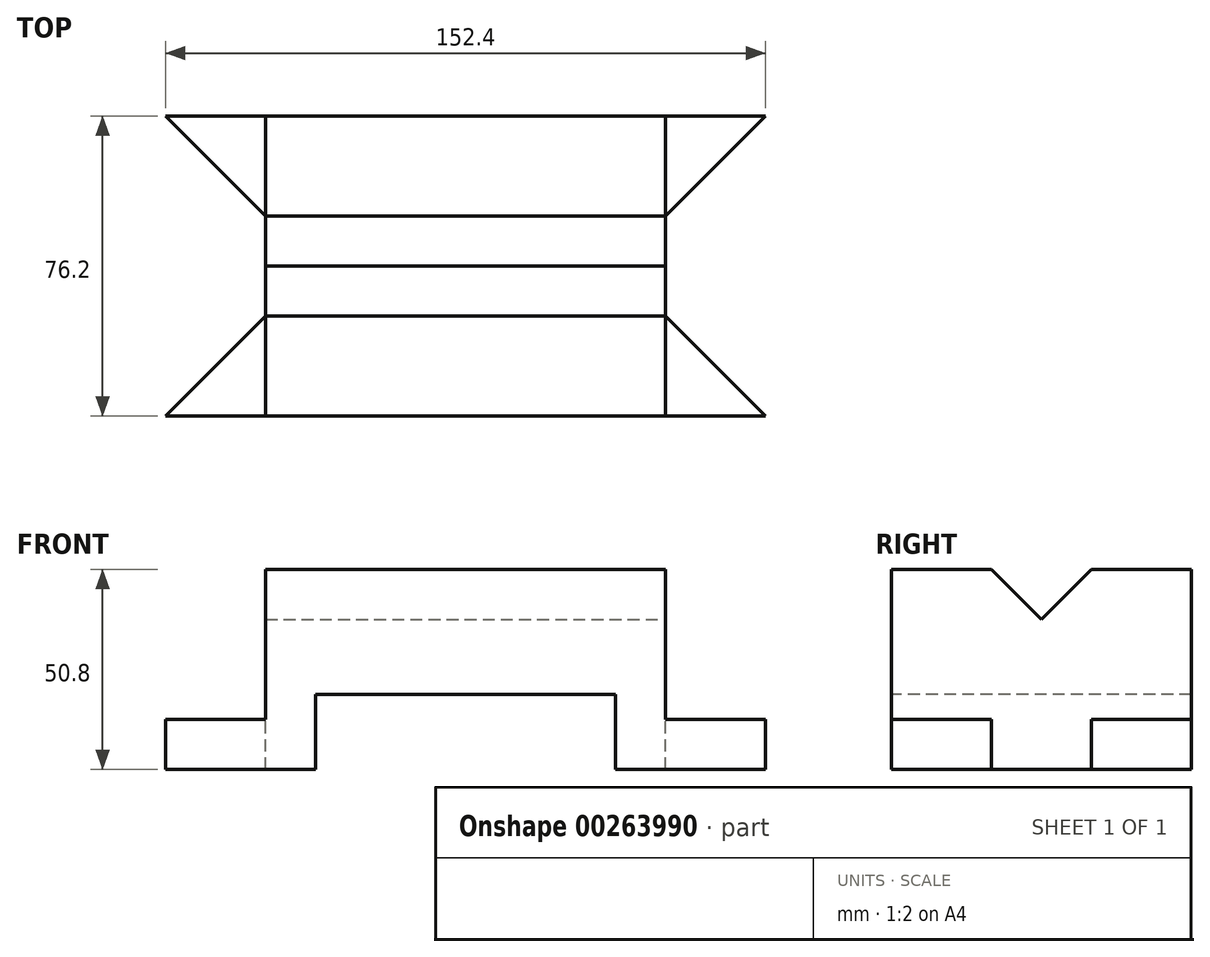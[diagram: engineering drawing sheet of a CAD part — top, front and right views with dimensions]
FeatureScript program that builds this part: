
annotation { "Feature Type Name" : "Feature", "Feature Type Description" : "" }
export const myFeature = defineFeature(function(context is Context, id is Id, definition is map)
    precondition{}
    {
        {
            var Q0;
            Q0=qCreatedBy(makeId("Front.planeOp"),FACE);
            var sketch = newSketch(context, id + "F0", { "sketchPlane" : qUnion([Q0])});
            skLineSegment(sketch, "E0", {"start": v(-76.43, 0) * mm, "end": v(-76.43, 12.7) * mm});
            skLineSegment(sketch, "E1", {"start": v(-76.43, 12.7) * mm, "end": v(-51.03, 12.7) * mm});
            skLineSegment(sketch, "E2", {"start": v(-51.03, 12.7) * mm, "end": v(-51.03, 50.8) * mm});
            skLineSegment(sketch, "E3", {"start": v(-51.03, 50.8) * mm, "end": v(50.57, 50.8) * mm});
            skLineSegment(sketch, "E4", {"start": v(50.57, 50.8) * mm, "end": v(50.57, 12.7) * mm});
            skLineSegment(sketch, "E5", {"start": v(50.57, 12.7) * mm, "end": v(75.97, 12.7) * mm});
            skLineSegment(sketch, "E6", {"start": v(75.97, 12.7) * mm, "end": v(75.97, 0) * mm});
            skLineSegment(sketch, "E7", {"start": v(75.97, 0) * mm, "end": v(37.87, 0) * mm});
            skLineSegment(sketch, "E8", {"start": v(37.87, 0) * mm, "end": v(37.87, 19.05) * mm});
            skLineSegment(sketch, "E9", {"start": v(37.87, 19.05) * mm, "end": v(-38.33, 19.05) * mm});
            skLineSegment(sketch, "E10", {"start": v(-38.33, 19.05) * mm, "end": v(-38.33, 0) * mm});
            skLineSegment(sketch, "E11", {"start": v(-38.33, 0) * mm, "end": v(-76.43, 0) * mm});
            skSolve(sketch);
        }
        {
            var Q0;
            Q0=makeQuery(id+"F0.imprint","IMPRINT",FACE,{"disambiguationData":[TD([[makeQuery(id+"F0.imprint","IMPRINT",EDGE,{"derivedFrom":sQuery(id+"F0.wireOp",EDGE,"E0")}),-1.0]])]});
            extrude(context, id + "F1", {"entities" : qUnion([Q0]), "oppositeDirection" : true, "depth" : 76.2 * mm});
        }
        {
            var Q0;
            Q0=makeQuery(id+"F1.opExtrude","SWEPT_FACE",FACE,{"disambiguationData":[OSD([sQuery(id+"F0.wireOp",EDGE,"E1")])]});
            var sketch = newSketch(context, id + "F2", { "sketchPlane" : qUnion([Q0])});
            skLineSegment(sketch, "E12", {"start": v(-51.03, 0) * mm, "end": v(-51.03, 25.4) * mm});
            skLineSegment(sketch, "E13", {"start": v(-51.03, 25.4) * mm, "end": v(-76.43, 0) * mm});
            skLineSegment(sketch, "E14", {"start": v(-51.03, 76.2) * mm, "end": v(-51.03, 50.8) * mm});
            skLineSegment(sketch, "E15", {"start": v(-51.03, 50.8) * mm, "end": v(-76.43, 76.2) * mm});
            skLineSegment(sketch, "E16", {"start": v(-76.43, 76.2) * mm, "end": v(-51.03, 76.2) * mm});
            skLineSegment(sketch, "E17", {"start": v(-76.43, 0) * mm, "end": v(-51.03, 0) * mm});
            skSolve(sketch);
        }
        {
            var Q0;
            {var subQ0=sQuery(id+"F2.wireOp",EDGE,"E13");Q0=makeQuery(id+"F2.imprint","IMPRINT",FACE,{"disambiguationData":[TD([[makeQuery(id+"F2.imprint","IMPRINT",EDGE,{"derivedFrom":subQ0}),-1.0]])]});}
            extrude(context, id + "F3", {"entities" : qUnion([Q0]), "operationType" : NewBodyOperationType.REMOVE, "endBound" : BoundingType.UP_TO_NEXT, "oppositeDirection" : true, "depth" : 25.4 * mm});
        }
        {
            var Q0;
            Q0=makeQuery(id+"F1.opExtrude","SWEPT_FACE",FACE,{"disambiguationData":[OSD([sQuery(id+"F0.wireOp",EDGE,"E5")])]});
            var sketch = newSketch(context, id + "F4", { "sketchPlane" : qUnion([Q0])});
            skLineSegment(sketch, "E18", {"start": v(50.57, 0) * mm, "end": v(75.97, 0) * mm});
            skLineSegment(sketch, "E19", {"start": v(50.57, 0) * mm, "end": v(50.57, 25.4) * mm});
            skLineSegment(sketch, "E20", {"start": v(50.57, 25.4) * mm, "end": v(75.97, 0) * mm});
            skLineSegment(sketch, "E21", {"start": v(50.57, 76.2) * mm, "end": v(50.57, 50.8) * mm});
            skLineSegment(sketch, "E22", {"start": v(50.57, 50.8) * mm, "end": v(75.97, 76.2) * mm});
            skLineSegment(sketch, "E23", {"start": v(75.97, 76.2) * mm, "end": v(50.57, 76.2) * mm});
            skSolve(sketch);
        }
        {
            var Q0;
            {var subQ0=sQuery(id+"F4.wireOp",EDGE,"E20");Q0=makeQuery(id+"F4.imprint","IMPRINT",FACE,{"disambiguationData":[TD([[makeQuery(id+"F4.imprint","IMPRINT",EDGE,{"derivedFrom":subQ0}),1.0]])]});}
            extrude(context, id + "F5", {"entities" : qUnion([Q0]), "operationType" : NewBodyOperationType.REMOVE, "endBound" : BoundingType.UP_TO_NEXT, "oppositeDirection" : true, "depth" : 25.4 * mm});
        }
        {
            var Q0;
            {var subQ0=sQuery(id+"F0.wireOp",EDGE,"E4");Q0=makeQuery(id+"F5.boolean.opBoolean","MERGE",FACE,{"derivedFrom":[makeQuery(id+"F1.opExtrude","SWEPT_FACE",FACE,{"disambiguationData":[OSD([subQ0])]}),makeQuery(id+"F5.opExtrude","SWEPT_FACE",FACE,{"disambiguationData":[OSD([subQ0,sQuery(id+"F0.wireOp",EDGE,"E5")])]})]});}
            var sketch = newSketch(context, id + "F6", { "sketchPlane" : qUnion([Q0])});
            skLineSegment(sketch, "E24", {"start": v(0, 50.8) * mm, "end": v(25.4, 50.8) * mm});
            skLineSegment(sketch, "E25", {"start": v(76.2, 50.8) * mm, "end": v(50.8, 50.8) * mm});
            skLineSegment(sketch, "E26", {"start": v(38.1, 38.1) * mm, "end": v(50.8, 50.8) * mm});
            skLineSegment(sketch, "E27", {"start": v(38.1, 38.1) * mm, "end": v(25.4, 50.8) * mm});
            skSolve(sketch);
        }
        {
            var Q0;
            {var subQ0=sQuery(id+"F6.wireOp",EDGE,"E26");Q0=makeQuery(id+"F6.imprint","IMPRINT",FACE,{"disambiguationData":[TD([[makeQuery(id+"F6.imprint","IMPRINT",EDGE,{"derivedFrom":subQ0}),1.0]])]});}
            extrude(context, id + "F7", {"entities" : qUnion([Q0]), "operationType" : NewBodyOperationType.REMOVE, "endBound" : BoundingType.UP_TO_NEXT, "oppositeDirection" : true, "depth" : 25.4 * mm});
        }
    });
